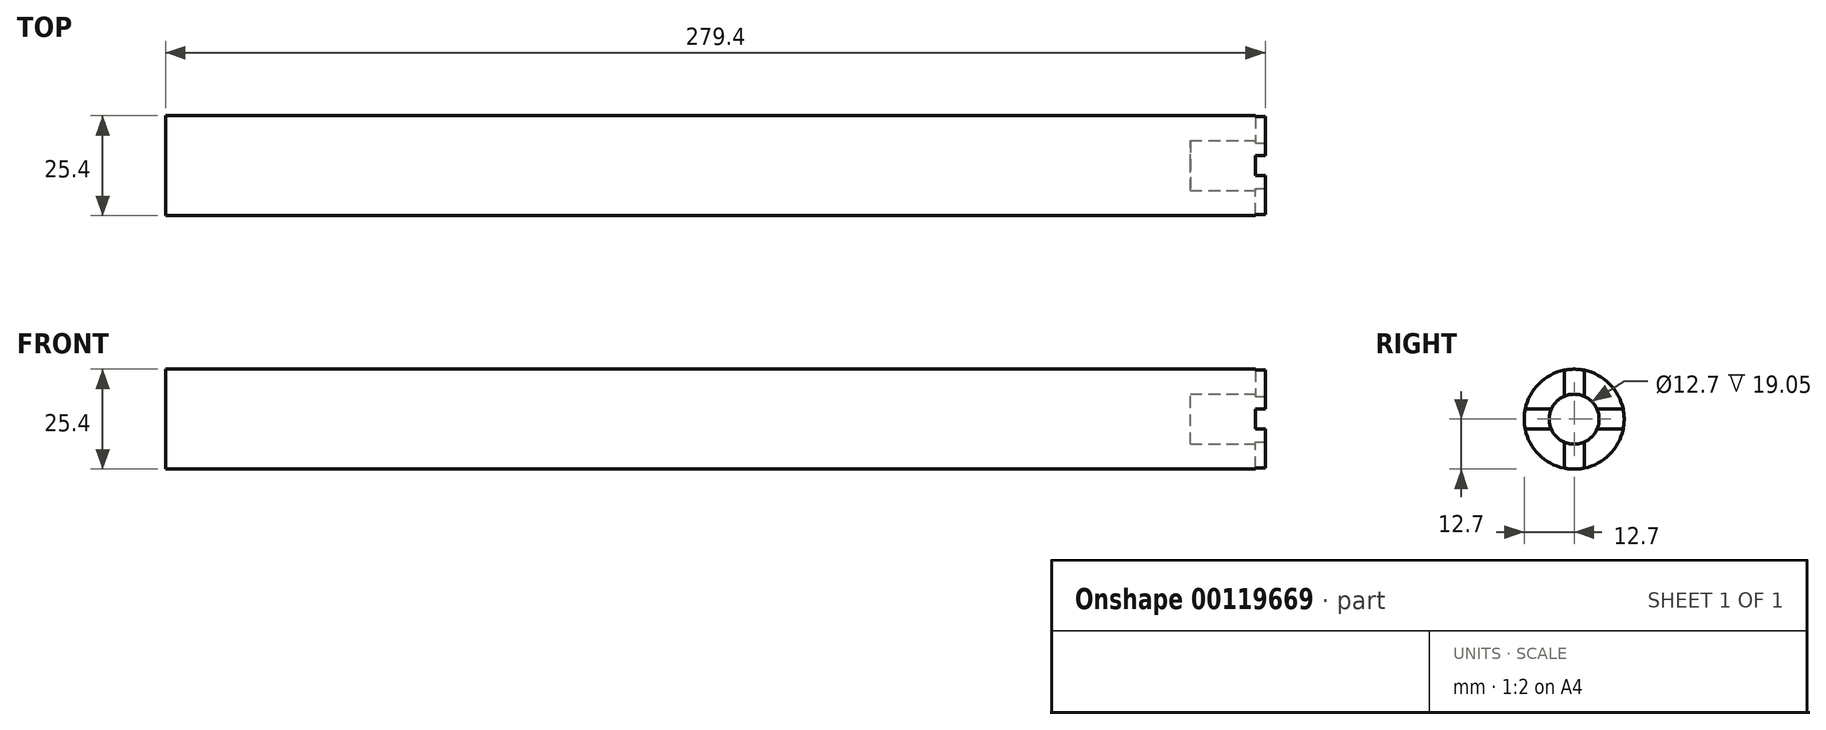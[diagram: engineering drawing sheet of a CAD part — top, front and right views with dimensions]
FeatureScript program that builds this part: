
annotation { "Feature Type Name" : "Feature", "Feature Type Description" : "" }
export const myFeature = defineFeature(function(context is Context, id is Id, definition is map)
    precondition{}
    {
        {
            var Q0;
            Q0=qCreatedBy(makeId("Front.planeOp"),FACE);
            var sketch = newSketch(context, id + "F0", { "sketchPlane" : qUnion([Q0])});
            skLineSegment(sketch, "E0.bottom", {"start": v(0, 0) * mm, "end": v(279.4, 0) * mm});
            skLineSegment(sketch, "E0.top", {"start": v(0, 12.7) * mm, "end": v(279.4, 12.7) * mm});
            skLineSegment(sketch, "E0.left", {"start": v(0, 0) * mm, "end": v(0, 12.7) * mm});
            skLineSegment(sketch, "E0.right", {"start": v(279.4, 0) * mm, "end": v(279.4, 12.7) * mm});
            skLineSegment(sketch, "E1", {"start": v(0, 0) * mm, "end": v(352, 0) * mm, "construction": true});
            skSolve(sketch);
        }
        {
            var Q0;
            Q0=makeQuery(id+"F0.imprint","IMPRINT",FACE,{"disambiguationData":[TD([[makeQuery(id+"F0.imprint","IMPRINT",EDGE,{"derivedFrom":sQuery(id+"F0.wireOp",EDGE,"E0.bottom")}),1.0]])]});
            var Q1;
            Q1=sQuery(id+"F0.wireOp",EDGE,"E1");
            revolve(context, id + "F1", {"entities" : qUnion([Q0]), "axis" : qUnion([Q1]), "revolveType" : RevolveType.FULL});
        }
        {
            var Q0;
            Q0=makeQuery(id+"F1.opRevolve","SWEPT_FACE",FACE,{"disambiguationData":[OSD([sQuery(id+"F0.wireOp",EDGE,"E0.right")])]});
            var sketch = newSketch(context, id + "F2", { "sketchPlane" : qUnion([Q0])});
            skCircle(sketch, "E2", {"center": v(0, 0) * mm, "radius": 6.35 * mm});
            skLineSegment(sketch, "E3", {"start": v(0, 12.7) * mm, "end": v(0, -12.7) * mm, "construction": true});
            skLineSegment(sketch, "E4", {"start": v(-12.7, 0) * mm, "end": v(12.7, 0) * mm, "construction": true});
            skLineSegment(sketch, "E5", {"start": v(-2.54, 12.44) * mm, "end": v(-2.54, 5.82) * mm});
            skLineSegment(sketch, "E6", {"start": v(2.54, 12.44) * mm, "end": v(2.54, 5.82) * mm});
            skLineSegment(sketch, "E7", {"start": v(12.44, 2.54) * mm, "end": v(5.82, 2.54) * mm});
            skLineSegment(sketch, "E8", {"start": v(12.44, -2.54) * mm, "end": v(5.82, -2.54) * mm});
            skLineSegment(sketch, "E9", {"start": v(-2.54, -12.44) * mm, "end": v(-2.54, -5.82) * mm});
            skLineSegment(sketch, "E10", {"start": v(2.54, -12.44) * mm, "end": v(2.54, -5.82) * mm});
            skLineSegment(sketch, "E11", {"start": v(-12.44, -2.54) * mm, "end": v(-5.82, -2.54) * mm});
            skLineSegment(sketch, "E12", {"start": v(-12.44, 2.54) * mm, "end": v(-5.82, 2.54) * mm});
            skSolve(sketch);
        }
        {
            var Q0;
            {var subQ0=sQuery(id+"F2.wireOp",EDGE,"E2");var subQ4=makeQuery(id+"F2.imprint","INTERSECT",VERTEX,{"derivedFrom":[subQ0,sQuery(id+"F2.wireOp",EDGE,"E6")]});Q0=makeQuery(id+"F2.imprint","IMPRINT",FACE,{"disambiguationData":[TD([[makeQuery(id+"F2.imprint","IMPRINT",EDGE,{"disambiguationData":[TD([[subQ4,1.0]])],"derivedFrom":subQ0}),1.0]])]});}
            extrude(context, id + "F3", {"entities" : qUnion([Q0]), "operationType" : NewBodyOperationType.REMOVE, "oppositeDirection" : true, "depth" : 19.05 * mm});
        }
        {
            var Q0;
            {var subQ0=sQuery(id+"F2.wireOp",EDGE,"E11");Q0=makeQuery(id+"F2.imprint","IMPRINT",FACE,{"disambiguationData":[TD([[makeQuery(id+"F2.imprint","IMPRINT",EDGE,{"derivedFrom":subQ0}),1.0]])]});}
            var Q1;
            {var subQ0=sQuery(id+"F2.wireOp",EDGE,"E7");Q1=makeQuery(id+"F2.imprint","IMPRINT",FACE,{"disambiguationData":[TD([[makeQuery(id+"F2.imprint","IMPRINT",EDGE,{"derivedFrom":subQ0}),1.0]])]});}
            var Q2;
            {var subQ0=sQuery(id+"F2.wireOp",EDGE,"E9");Q2=makeQuery(id+"F2.imprint","IMPRINT",FACE,{"disambiguationData":[TD([[makeQuery(id+"F2.imprint","IMPRINT",EDGE,{"derivedFrom":subQ0}),-1.0]])]});}
            var Q3;
            {var subQ0=sQuery(id+"F2.wireOp",EDGE,"E5");Q3=makeQuery(id+"F2.imprint","IMPRINT",FACE,{"disambiguationData":[TD([[makeQuery(id+"F2.imprint","IMPRINT",EDGE,{"derivedFrom":subQ0}),1.0]])]});}
            extrude(context, id + "F4", {"entities" : qUnion([Q0, Q1, Q2, Q3]), "operationType" : NewBodyOperationType.REMOVE, "oppositeDirection" : true, "depth" : 2.54 * mm});
        }
    });
